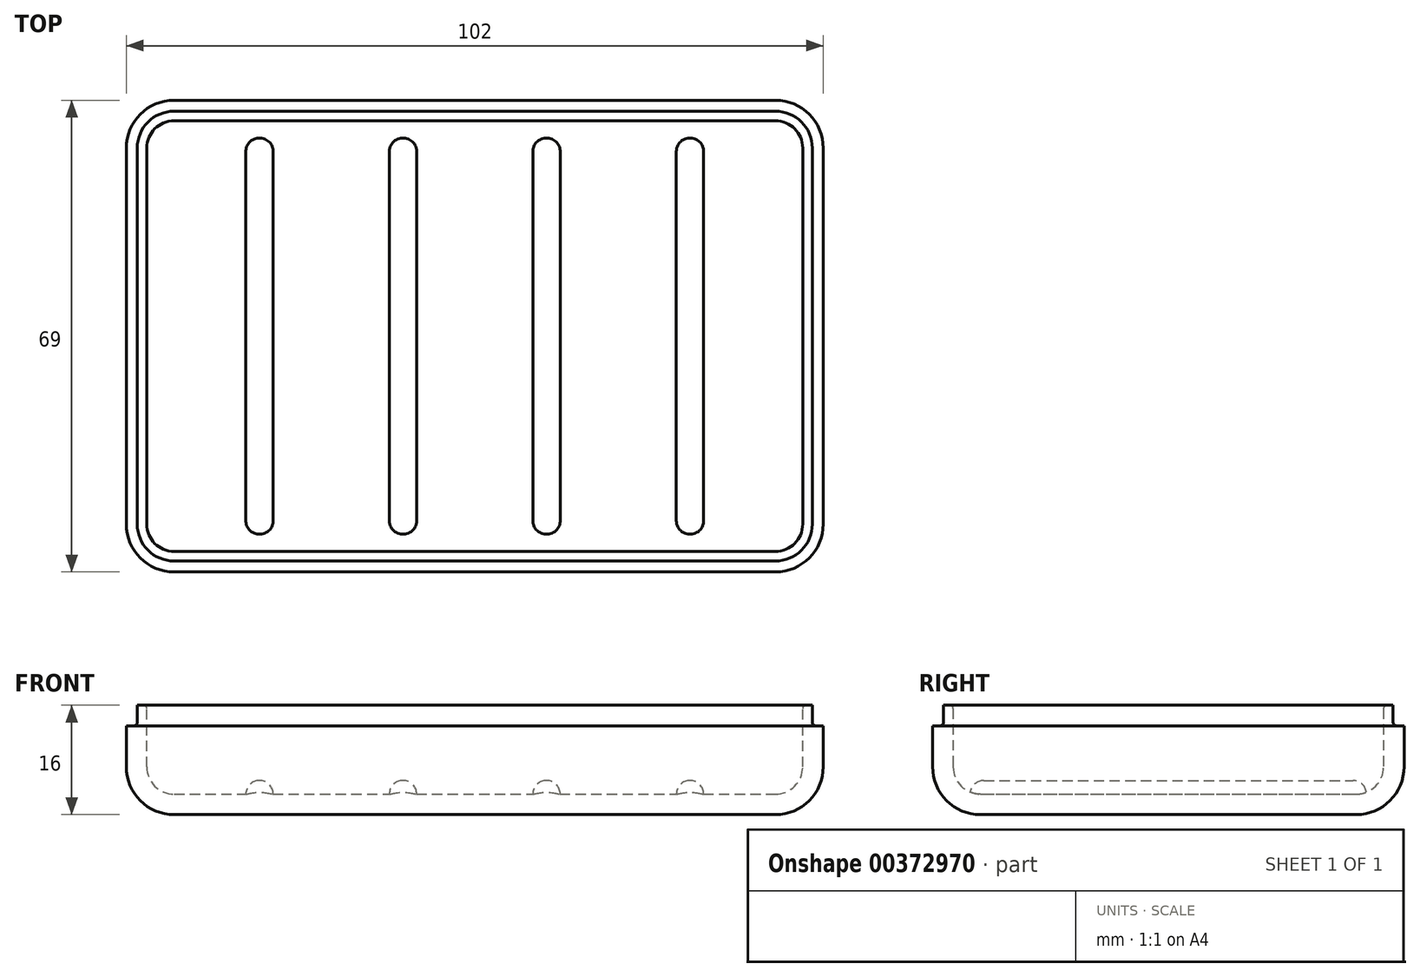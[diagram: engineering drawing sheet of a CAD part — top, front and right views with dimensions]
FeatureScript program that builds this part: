
annotation { "Feature Type Name" : "Feature", "Feature Type Description" : "" }
export const myFeature = defineFeature(function(context is Context, id is Id, definition is map)
    precondition{}
    {
        {
            var Q0;
            Q0=qCreatedBy(makeId("Top.planeOp"),FACE);
            var sketch = newSketch(context, id + "F0", { "sketchPlane" : qUnion([Q0])});
            skLineSegment(sketch, "E0.bottom", {"start": v(44, -34.5) * mm, "end": v(-44, -34.5) * mm});
            skLineSegment(sketch, "E0.top", {"start": v(44, 34.5) * mm, "end": v(-44, 34.5) * mm});
            skLineSegment(sketch, "E0.left", {"start": v(51, -27.5) * mm, "end": v(51, 27.5) * mm});
            skLineSegment(sketch, "E0.right", {"start": v(-51, -27.5) * mm, "end": v(-51, 27.5) * mm});
            skPoint(sketch, "E0.middle", {"position": v(0, 0) * mm});
            skLineSegment(sketch, "E1.bottom", {"start": v(-44, 27.5) * mm, "end": v(44, 27.5) * mm, "construction": true});
            skLineSegment(sketch, "E1.top", {"start": v(-44, -27.5) * mm, "end": v(44, -27.5) * mm, "construction": true});
            skLineSegment(sketch, "E1.left", {"start": v(-44, 27.5) * mm, "end": v(-44, -27.5) * mm, "construction": true});
            skLineSegment(sketch, "E1.right", {"start": v(44, 27.5) * mm, "end": v(44, -27.5) * mm, "construction": true});
            skPoint(sketch, "E2.visualSharp", {"position": v(-51, 34.5) * mm});
            skArc(sketch, "E2.filletArc", {"start": v(-44, 34.5) * mm, "mid": v(-48.95, 32.45) * mm, "end": v(-51, 27.5) * mm});
            skPoint(sketch, "E3.visualSharp", {"position": v(-51, -34.5) * mm});
            skArc(sketch, "E3.filletArc", {"start": v(-51, -27.5) * mm, "mid": v(-48.95, -32.45) * mm, "end": v(-44, -34.5) * mm});
            skPoint(sketch, "E4.visualSharp", {"position": v(51, -34.5) * mm});
            skArc(sketch, "E4.filletArc", {"start": v(44, -34.5) * mm, "mid": v(48.95, -32.45) * mm, "end": v(51, -27.5) * mm});
            skPoint(sketch, "E5.visualSharp", {"position": v(51, 34.5) * mm});
            skArc(sketch, "E5.filletArc", {"start": v(51, 27.5) * mm, "mid": v(48.95, 32.45) * mm, "end": v(44, 34.5) * mm});
            skSolve(sketch);
        }
        {
            var Q0;
            Q0=makeQuery(id+"F0.imprint","IMPRINT",FACE,{"disambiguationData":[TD([[makeQuery(id+"F0.imprint","IMPRINT",EDGE,{"derivedFrom":sQuery(id+"F0.wireOp",EDGE,"E0.bottom")}),-1.0]])]});
            extrude(context, id + "F1", {"entities" : qUnion([Q0]), "depth" : 16 * mm});
        }
        {
            var Q0;
            Q0=makeQuery(id+"F1.opExtrude","CAP_EDGE",EDGE,{"disambiguationData":[OSD([sQuery(id+"F0.wireOp",EDGE,"E0.bottom")])],"isStart":true});
            fillet(context, id + "F2", {"entities" : qUnion([Q0]), "radius" : 7 * mm, "tangentPropagation" : true, "allowEdgeOverflow" : false});
        }
        {
            var Q0;
            Q0=makeQuery(id+"F1.opExtrude","CAP_FACE",FACE,{"disambiguationData":[OSD([sQuery(id+"F0.wireOp",EDGE,"E0.bottom"),sQuery(id+"F0.wireOp",EDGE,"E0.top"),sQuery(id+"F0.wireOp",EDGE,"E0.left"),sQuery(id+"F0.wireOp",EDGE,"E0.right"),sQuery(id+"F0.wireOp",EDGE,"E2.filletArc"),sQuery(id+"F0.wireOp",EDGE,"E3.filletArc"),sQuery(id+"F0.wireOp",EDGE,"E4.filletArc"),sQuery(id+"F0.wireOp",EDGE,"E5.filletArc")])],"isStart":false});
            shell(context, id + "F3", {"entities" : qUnion([Q0]), "thickness" : 3 * mm});
        }
        {
            var Q0;
            Q0=makeQuery(id+"F3.opShell","OFFSET_FACE",FACE,{"disambiguationData":[OSD([sQuery(id+"F0.wireOp",EDGE,"E0.bottom"),sQuery(id+"F0.wireOp",EDGE,"E0.top"),sQuery(id+"F0.wireOp",EDGE,"E0.left"),sQuery(id+"F0.wireOp",EDGE,"E0.right"),sQuery(id+"F0.wireOp",EDGE,"E2.filletArc"),sQuery(id+"F0.wireOp",EDGE,"E3.filletArc"),sQuery(id+"F0.wireOp",EDGE,"E4.filletArc"),sQuery(id+"F0.wireOp",EDGE,"E5.filletArc")])]});
            var sketch = newSketch(context, id + "F4", { "sketchPlane" : qUnion([Q0])});
            skLineSegment(sketch, "E6.bottom", {"start": v(10.5, 29) * mm, "end": v(10.5, 29) * mm});
            skLineSegment(sketch, "E6.top", {"start": v(10.5, -29) * mm, "end": v(10.5, -29) * mm});
            skLineSegment(sketch, "E6.left", {"start": v(12.5, 27) * mm, "end": v(12.5, -27) * mm});
            skLineSegment(sketch, "E6.right", {"start": v(8.5, 27) * mm, "end": v(8.5, -27) * mm});
            skPoint(sketch, "E6.middle", {"position": v(10.5, 0) * mm});
            skLineSegment(sketch, "E7.bottom", {"start": v(31.5, 29) * mm, "end": v(31.5, 29) * mm});
            skLineSegment(sketch, "E7.top", {"start": v(31.5, -29) * mm, "end": v(31.5, -29) * mm});
            skLineSegment(sketch, "E7.left", {"start": v(33.5, 27) * mm, "end": v(33.5, -27) * mm});
            skLineSegment(sketch, "E7.right", {"start": v(29.5, 27) * mm, "end": v(29.5, -27) * mm});
            skPoint(sketch, "E7.middle", {"position": v(31.5, 0) * mm});
            skLineSegment(sketch, "E8.bottom", {"start": v(-31.5, -29) * mm, "end": v(-31.5, -29) * mm});
            skLineSegment(sketch, "E8.top", {"start": v(-31.5, 29) * mm, "end": v(-31.5, 29) * mm});
            skLineSegment(sketch, "E8.left", {"start": v(-29.5, -27) * mm, "end": v(-29.5, 27) * mm});
            skLineSegment(sketch, "E8.right", {"start": v(-33.5, -27) * mm, "end": v(-33.5, 27) * mm});
            skPoint(sketch, "E8.middle", {"position": v(-31.5, 0) * mm});
            skLineSegment(sketch, "E9.bottom", {"start": v(-10.5, -29) * mm, "end": v(-10.5, -29) * mm});
            skLineSegment(sketch, "E9.top", {"start": v(-10.5, 29) * mm, "end": v(-10.5, 29) * mm});
            skLineSegment(sketch, "E9.left", {"start": v(-8.5, -27) * mm, "end": v(-8.5, 27) * mm});
            skLineSegment(sketch, "E9.right", {"start": v(-12.5, -27) * mm, "end": v(-12.5, 27) * mm});
            skPoint(sketch, "E9.middle", {"position": v(-10.5, 0) * mm});
            skPoint(sketch, "E10.visualSharp", {"position": v(-33.5, 29) * mm});
            skArc(sketch, "E10.filletArc", {"start": v(-31.5, 29) * mm, "mid": v(-32.91, 28.41) * mm, "end": v(-33.5, 27) * mm});
            skPoint(sketch, "E11.visualSharp", {"position": v(-29.5, 29) * mm});
            skArc(sketch, "E11.filletArc", {"start": v(-29.5, 27) * mm, "mid": v(-30.09, 28.41) * mm, "end": v(-31.5, 29) * mm});
            skPoint(sketch, "E12.visualSharp", {"position": v(-12.5, 29) * mm});
            skArc(sketch, "E12.filletArc", {"start": v(-10.5, 29) * mm, "mid": v(-11.91, 28.41) * mm, "end": v(-12.5, 27) * mm});
            skPoint(sketch, "E13.visualSharp", {"position": v(-8.5, 29) * mm});
            skArc(sketch, "E13.filletArc", {"start": v(-8.5, 27) * mm, "mid": v(-9.09, 28.41) * mm, "end": v(-10.5, 29) * mm});
            skPoint(sketch, "E14.visualSharp", {"position": v(8.5, 29) * mm});
            skArc(sketch, "E14.filletArc", {"start": v(10.5, 29) * mm, "mid": v(9.09, 28.41) * mm, "end": v(8.5, 27) * mm});
            skPoint(sketch, "E15.visualSharp", {"position": v(12.5, 29) * mm});
            skArc(sketch, "E15.filletArc", {"start": v(12.5, 27) * mm, "mid": v(11.91, 28.41) * mm, "end": v(10.5, 29) * mm});
            skPoint(sketch, "E16.visualSharp", {"position": v(29.5, 29) * mm});
            skArc(sketch, "E16.filletArc", {"start": v(31.5, 29) * mm, "mid": v(30.09, 28.41) * mm, "end": v(29.5, 27) * mm});
            skPoint(sketch, "E17.visualSharp", {"position": v(33.5, 29) * mm});
            skArc(sketch, "E17.filletArc", {"start": v(33.5, 27) * mm, "mid": v(32.91, 28.41) * mm, "end": v(31.5, 29) * mm});
            skPoint(sketch, "E18.visualSharp", {"position": v(33.5, -29) * mm});
            skArc(sketch, "E18.filletArc", {"start": v(31.5, -29) * mm, "mid": v(32.91, -28.41) * mm, "end": v(33.5, -27) * mm});
            skPoint(sketch, "E19.visualSharp", {"position": v(29.5, -29) * mm});
            skArc(sketch, "E19.filletArc", {"start": v(29.5, -27) * mm, "mid": v(30.09, -28.41) * mm, "end": v(31.5, -29) * mm});
            skPoint(sketch, "E20.visualSharp", {"position": v(12.5, -29) * mm});
            skArc(sketch, "E20.filletArc", {"start": v(10.5, -29) * mm, "mid": v(11.91, -28.41) * mm, "end": v(12.5, -27) * mm});
            skPoint(sketch, "E21.visualSharp", {"position": v(8.5, -29) * mm});
            skArc(sketch, "E21.filletArc", {"start": v(8.5, -27) * mm, "mid": v(9.09, -28.41) * mm, "end": v(10.5, -29) * mm});
            skPoint(sketch, "E22.visualSharp", {"position": v(-8.5, -29) * mm});
            skArc(sketch, "E22.filletArc", {"start": v(-10.5, -29) * mm, "mid": v(-9.09, -28.41) * mm, "end": v(-8.5, -27) * mm});
            skPoint(sketch, "E23.visualSharp", {"position": v(-12.5, -29) * mm});
            skArc(sketch, "E23.filletArc", {"start": v(-12.5, -27) * mm, "mid": v(-11.91, -28.41) * mm, "end": v(-10.5, -29) * mm});
            skPoint(sketch, "E24.visualSharp", {"position": v(-29.5, -29) * mm});
            skArc(sketch, "E24.filletArc", {"start": v(-31.5, -29) * mm, "mid": v(-30.09, -28.41) * mm, "end": v(-29.5, -27) * mm});
            skPoint(sketch, "E25.visualSharp", {"position": v(-33.5, -29) * mm});
            skArc(sketch, "E25.filletArc", {"start": v(-33.5, -27) * mm, "mid": v(-32.91, -28.41) * mm, "end": v(-31.5, -29) * mm});
            skSolve(sketch);
        }
        {
            var Q0;
            Q0 = qSketchRegion(id + "F4", true);
            extrude(context, id + "F5", {"entities" : qUnion([Q0]), "operationType" : NewBodyOperationType.ADD, "depth" : 2 * mm});
        }
        {
            var Q0;
            Q0=makeQuery(id+"F5.opExtrude","CAP_EDGE",EDGE,{"disambiguationData":[OSD([sQuery(id+"F4.wireOp",EDGE,"E7.right")])],"isStart":false});
            var Q1;
            Q1=makeQuery(id+"F5.opExtrude","CAP_EDGE",EDGE,{"disambiguationData":[OSD([sQuery(id+"F4.wireOp",EDGE,"E6.right")])],"isStart":false});
            var Q2;
            Q2=makeQuery(id+"F5.opExtrude","CAP_EDGE",EDGE,{"disambiguationData":[OSD([sQuery(id+"F4.wireOp",EDGE,"E9.right")])],"isStart":false});
            var Q3;
            Q3=makeQuery(id+"F5.opExtrude","CAP_EDGE",EDGE,{"disambiguationData":[OSD([sQuery(id+"F4.wireOp",EDGE,"E8.right")])],"isStart":false});
            fillet(context, id + "F6", {"entities" : qUnion([Q0, Q1, Q2, Q3]), "radius" : 2 * mm, "tangentPropagation" : true, "allowEdgeOverflow" : false});
        }
        {
            var Q0;
            Q0=makeQuery(id+"F1.opExtrude","CAP_FACE",FACE,{"disambiguationData":[OSD([sQuery(id+"F0.wireOp",EDGE,"E0.bottom"),sQuery(id+"F0.wireOp",EDGE,"E0.top"),sQuery(id+"F0.wireOp",EDGE,"E0.left"),sQuery(id+"F0.wireOp",EDGE,"E0.right"),sQuery(id+"F0.wireOp",EDGE,"E2.filletArc"),sQuery(id+"F0.wireOp",EDGE,"E3.filletArc"),sQuery(id+"F0.wireOp",EDGE,"E4.filletArc"),sQuery(id+"F0.wireOp",EDGE,"E5.filletArc")])],"isStart":false});
            var sketch = newSketch(context, id + "F7", { "sketchPlane" : qUnion([Q0])});
            skArc(sketch, "E26.0", {"start": v(-44, 34.5) * mm, "mid": v(-48.95, 32.45) * mm, "end": v(-51, 27.5) * mm});
            skLineSegment(sketch, "E27.0", {"start": v(44, 34.5) * mm, "end": v(-44, 34.5) * mm});
            skLineSegment(sketch, "E28.0", {"start": v(-51, -27.5) * mm, "end": v(-51, 27.5) * mm});
            skArc(sketch, "E29.0", {"start": v(-51, -27.5) * mm, "mid": v(-48.95, -32.45) * mm, "end": v(-44, -34.5) * mm});
            skLineSegment(sketch, "E30.0", {"start": v(44, -34.5) * mm, "end": v(-44, -34.5) * mm});
            skArc(sketch, "E31.0", {"start": v(44, -34.5) * mm, "mid": v(48.95, -32.45) * mm, "end": v(51, -27.5) * mm});
            skLineSegment(sketch, "E32.0", {"start": v(51, -27.5) * mm, "end": v(51, 27.5) * mm});
            skArc(sketch, "E33.0", {"start": v(51, 27.5) * mm, "mid": v(48.95, 32.45) * mm, "end": v(44, 34.5) * mm});
            skArc(sketch, "E34.0", {"start": v(49.4, 27.5) * mm, "mid": v(47.82, 31.32) * mm, "end": v(44, 32.9) * mm});
            skLineSegment(sketch, "E34.1", {"start": v(49.4, -27.5) * mm, "end": v(49.4, 27.5) * mm});
            skLineSegment(sketch, "E34.2", {"start": v(44, 32.9) * mm, "end": v(-44, 32.9) * mm});
            skArc(sketch, "E34.3", {"start": v(44, -32.9) * mm, "mid": v(47.82, -31.32) * mm, "end": v(49.4, -27.5) * mm});
            skArc(sketch, "E34.4", {"start": v(-44, 32.9) * mm, "mid": v(-47.82, 31.32) * mm, "end": v(-49.4, 27.5) * mm});
            skLineSegment(sketch, "E34.5", {"start": v(-49.4, -27.5) * mm, "end": v(-49.4, 27.5) * mm});
            skArc(sketch, "E34.6", {"start": v(-49.4, -27.5) * mm, "mid": v(-47.82, -31.32) * mm, "end": v(-44, -32.9) * mm});
            skLineSegment(sketch, "E34.7", {"start": v(44, -32.9) * mm, "end": v(-44, -32.9) * mm});
            skSolve(sketch);
        }
        {
            var Q0;
            Q0 = qSketchRegion(id + "F7", true);
            extrude(context, id + "F8", {"entities" : qUnion([Q0]), "operationType" : NewBodyOperationType.REMOVE, "oppositeDirection" : true, "depth" : 3 * mm});
        }
        {
            var Q0;
            Q0=makeQuery(id+"F8.boolean.opBoolean","COPY",EDGE,{"derivedFrom":makeQuery(id+"F8.opExtrude","CAP_EDGE",EDGE,{"disambiguationData":[OSD([sQuery(id+"F7.wireOp",EDGE,"E34.1")])],"isStart":true})});
            var Q1;
            {var subQ0=sQuery(id+"F0.wireOp",EDGE,"E0.bottom");Q1=makeQuery(id+"F3.opShell","OFFSET_EDGE",EDGE,{"disambiguationData":[OSD([subQ0]),TDD([makeQuery(id+"F1.opExtrude","CAP_EDGE",EDGE,{"disambiguationData":[OSD([subQ0])],"isStart":false})])]});}
            var Q2;
            Q2=makeQuery(id+"F8.boolean.opBoolean","COPY",EDGE,{"derivedFrom":makeQuery(id+"F8.opExtrude","CAP_EDGE",EDGE,{"disambiguationData":[OSD([sQuery(id+"F7.wireOp",EDGE,"E34.7")])],"isStart":false})});
            fillet(context, id + "F9", {"entities" : qUnion([Q0, Q1, Q2]), "radius" : 0.5 * mm, "tangentPropagation" : true, "allowEdgeOverflow" : false});
        }
    });
